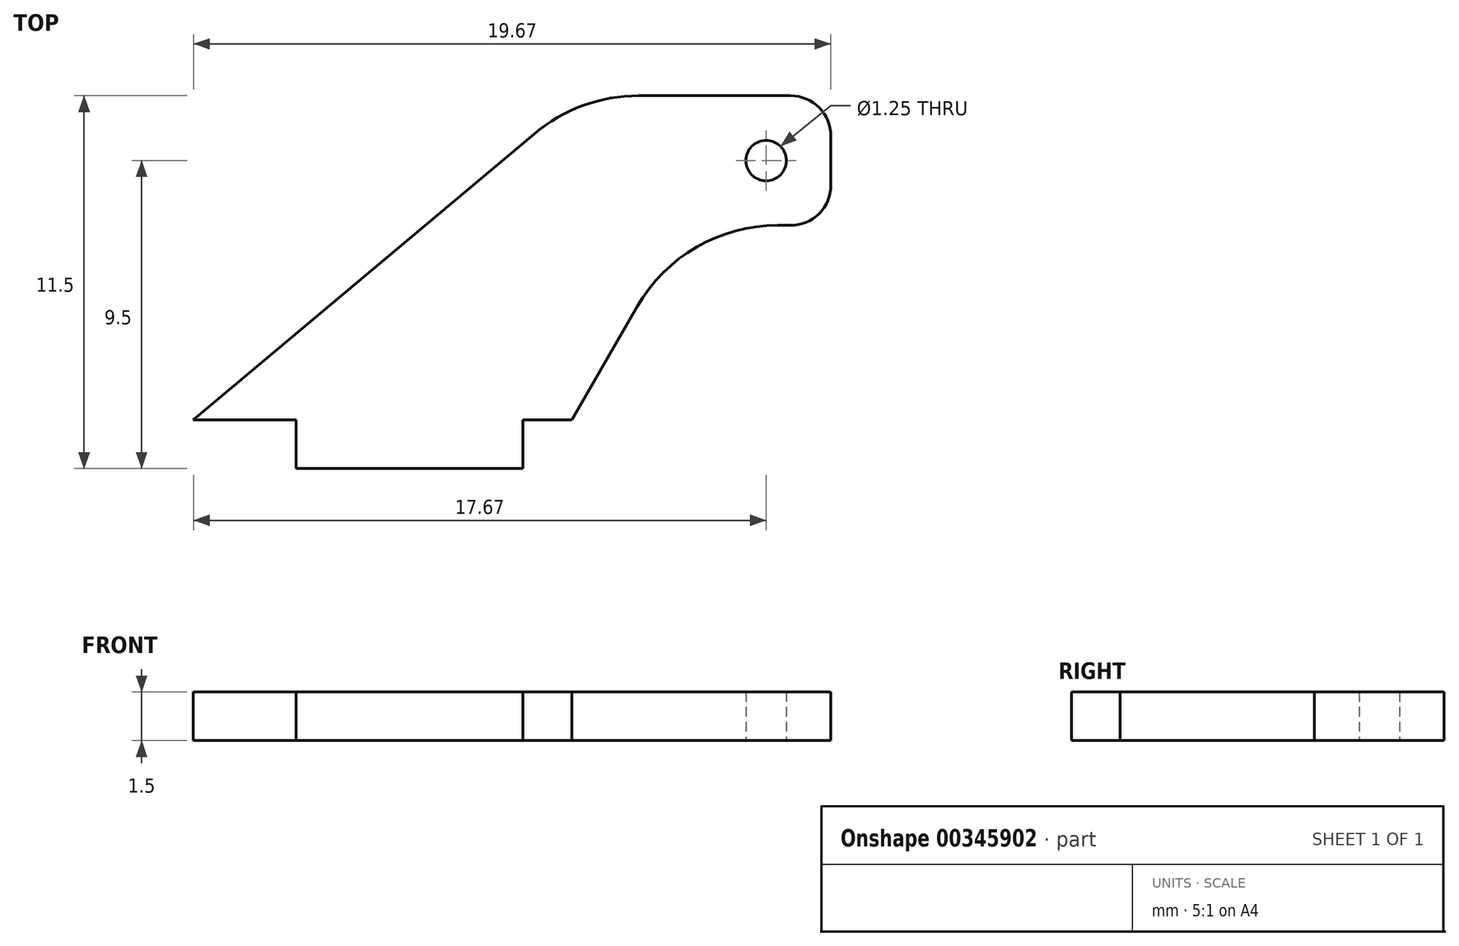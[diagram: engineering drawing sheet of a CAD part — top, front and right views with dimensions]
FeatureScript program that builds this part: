
annotation { "Feature Type Name" : "Feature", "Feature Type Description" : "" }
export const myFeature = defineFeature(function(context is Context, id is Id, definition is map)
    precondition{}
    {
        {
            var Q0;
            Q0=qCreatedBy(makeId("Top.planeOp"),FACE);
            var sketch = newSketch(context, id + "F0", { "sketchPlane" : qUnion([Q0])});
            skLineSegment(sketch, "E0", {"start": v(0, 0) * mm, "end": v(-3.18, 0) * mm});
            skLineSegment(sketch, "E1", {"start": v(-3.18, 0) * mm, "end": v(7.35, 8.83) * mm});
            skLineSegment(sketch, "E2", {"start": v(10.56, 10) * mm, "end": v(15.25, 10) * mm});
            skLineSegment(sketch, "E3", {"start": v(16.5, 8.75) * mm, "end": v(16.5, 7.25) * mm});
            skLineSegment(sketch, "E4", {"start": v(15.25, 6) * mm, "end": v(14.85, 6) * mm});
            skLineSegment(sketch, "E5", {"start": v(10.52, 3.5) * mm, "end": v(8.5, 0) * mm});
            skLineSegment(sketch, "E6", {"start": v(0, -1.5) * mm, "end": v(0, 0) * mm});
            skPoint(sketch, "E7.visualSharp", {"position": v(11.96, 6) * mm});
            skArc(sketch, "E7.filletArc", {"start": v(14.85, 6) * mm, "mid": v(12.35, 5.33) * mm, "end": v(10.52, 3.5) * mm});
            skPoint(sketch, "E8.visualSharp", {"position": v(16.5, 6) * mm});
            skArc(sketch, "E8.filletArc", {"start": v(15.25, 6) * mm, "mid": v(16.13, 6.37) * mm, "end": v(16.5, 7.25) * mm});
            skPoint(sketch, "E9.visualSharp", {"position": v(16.5, 10) * mm});
            skArc(sketch, "E9.filletArc", {"start": v(16.5, 8.75) * mm, "mid": v(16.13, 9.63) * mm, "end": v(15.25, 10) * mm});
            skPoint(sketch, "E10.visualSharp", {"position": v(8.74, 10) * mm});
            skArc(sketch, "E10.filletArc", {"start": v(10.56, 10) * mm, "mid": v(8.85, 9.7) * mm, "end": v(7.35, 8.83) * mm});
            skCircle(sketch, "E11", {"center": v(14.5, 8) * mm, "radius": 0.62 * mm});
            skLineSegment(sketch, "E12", {"start": v(8.5, 0) * mm, "end": v(7, 0) * mm});
            skLineSegment(sketch, "E13", {"start": v(7, 0) * mm, "end": v(7, -1.5) * mm});
            skLineSegment(sketch, "E14", {"start": v(7, -1.5) * mm, "end": v(0, -1.5) * mm});
            skSolve(sketch);
        }
        {
            var Q0;
            Q0=makeQuery(id+"F0.imprint","IMPRINT",FACE,{"disambiguationData":[TD([[makeQuery(id+"F0.imprint","IMPRINT",EDGE,{"derivedFrom":sQuery(id+"F0.wireOp",EDGE,"E0")}),-1.0]])]});
            extrude(context, id + "F1", {"entities" : qUnion([Q0]), "depth" : 1.5 * mm});
        }
    });
